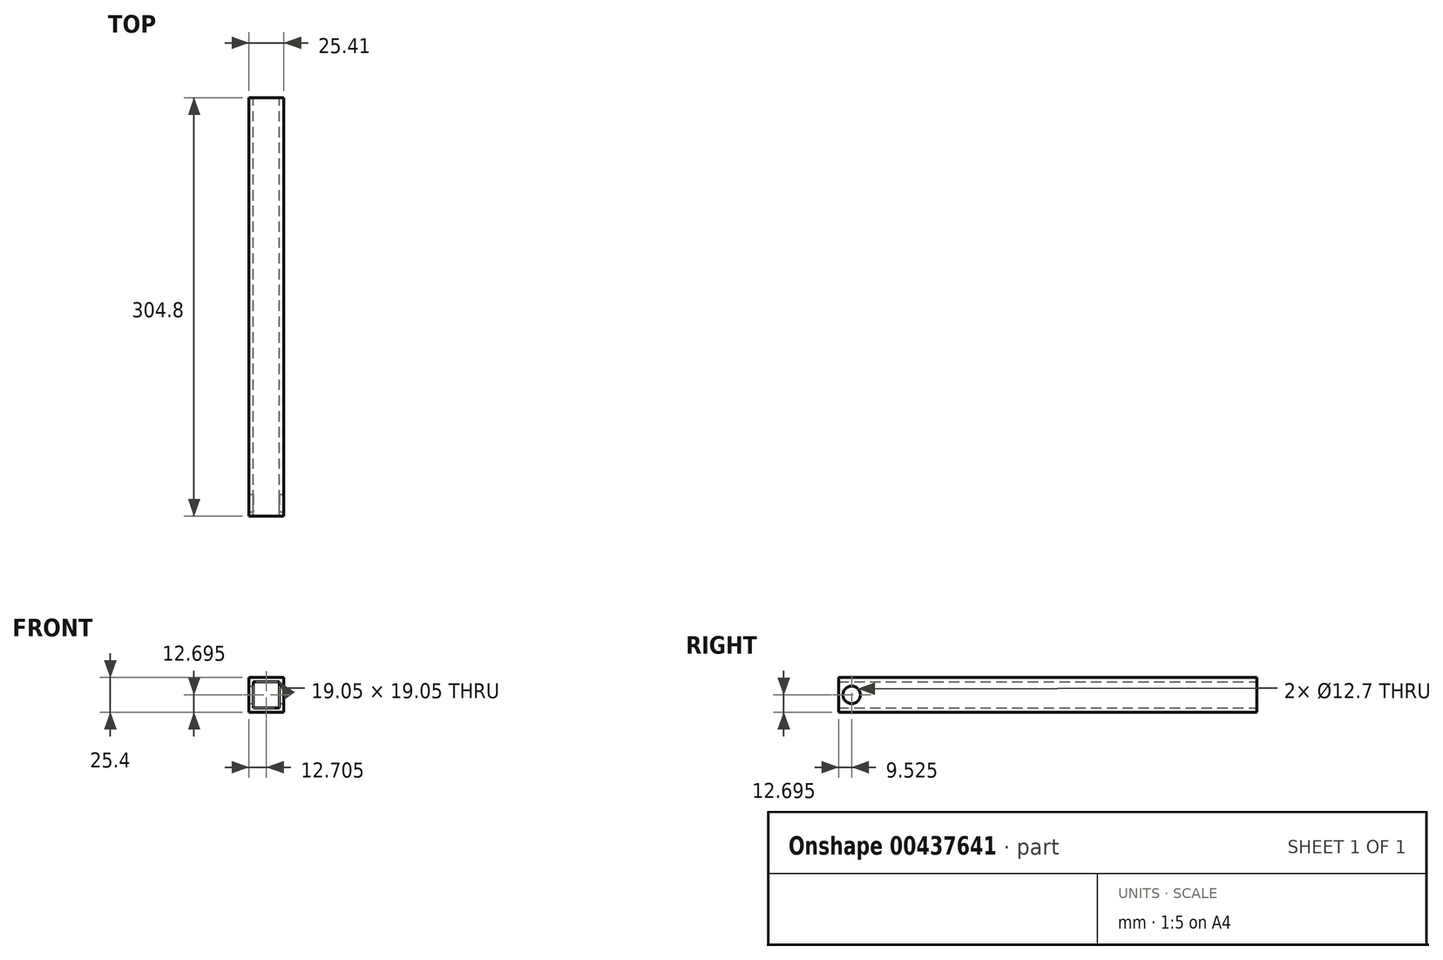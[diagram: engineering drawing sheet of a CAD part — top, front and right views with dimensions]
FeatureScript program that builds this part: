
annotation { "Feature Type Name" : "Feature", "Feature Type Description" : "" }
export const myFeature = defineFeature(function(context is Context, id is Id, definition is map)
    precondition{}
    {
        {
            var Q0;
            Q0=qCreatedBy(makeId("Front.planeOp"),FACE);
            var sketch = newSketch(context, id + "F0", { "sketchPlane" : qUnion([Q0])});
            skLineSegment(sketch, "E0.bottom", {"start": v(-22.23, 22.23) * mm, "end": v(3.17, 22.23) * mm});
            skLineSegment(sketch, "E0.top", {"start": v(-22.23, -3.18) * mm, "end": v(3.18, -3.18) * mm});
            skLineSegment(sketch, "E0.left", {"start": v(-22.23, 22.23) * mm, "end": v(-22.23, -3.18) * mm});
            skLineSegment(sketch, "E0.right", {"start": v(3.17, 22.23) * mm, "end": v(3.18, -3.18) * mm});
            skLineSegment(sketch, "E1.bottom", {"start": v(-19.05, 19.05) * mm, "end": v(0, 19.05) * mm});
            skLineSegment(sketch, "E1.top", {"start": v(-19.05, 0) * mm, "end": v(0, 0) * mm});
            skLineSegment(sketch, "E1.left", {"start": v(-19.05, 19.05) * mm, "end": v(-19.05, 0) * mm});
            skLineSegment(sketch, "E1.right", {"start": v(0, 19.05) * mm, "end": v(0, 0) * mm});
            skSolve(sketch);
        }
        {
            var Q0;
            Q0=qSketchRegion(id+"F0",true);
            extrude(context, id + "F1", {"entities" : qUnion([Q0]), "depth" : 304.8 * mm});
        }
        {
            var Q0;
            Q0=makeQuery(id+"F1.opExtrude","SWEPT_FACE",FACE,{"disambiguationData":[OSD([sQuery(id+"F0.wireOp",EDGE,"E0.right")])]});
            var sketch = newSketch(context, id + "F2", { "sketchPlane" : qUnion([Q0])});
            skLineSegment(sketch, "E2.bottom", {"start": v(-304.8, 22.23) * mm, "end": v(-295.28, 22.23) * mm});
            skLineSegment(sketch, "E2.top", {"start": v(-304.8, 9.52) * mm, "end": v(-295.28, 9.52) * mm});
            skLineSegment(sketch, "E2.left", {"start": v(-304.8, 22.23) * mm, "end": v(-304.8, 9.52) * mm});
            skLineSegment(sketch, "E2.right", {"start": v(-295.28, 22.23) * mm, "end": v(-295.28, 9.52) * mm});
            skSolve(sketch);
        }
        {
            var Q0;
            Q0=sQuery(id+"F2.wireOp",VERTEX,"HHmvUL8G-0XSV-ua7Z-FtjQ-vSaVrf7iGfoh.top.end");
            var Q1;
            Q1=sQuery(id+"F2.wireOp",VERTEX,"E2.top.end");
            var Q2;
            Q2=makeQuery(id+"F1.opExtrude","SWEPT_BODY",BODY,{"disambiguationData":[OSD([sQuery(id+"F0.wireOp",EDGE,"E0.bottom"),sQuery(id+"F0.wireOp",EDGE,"E0.top"),sQuery(id+"F0.wireOp",EDGE,"E0.left"),sQuery(id+"F0.wireOp",EDGE,"E0.right"),sQuery(id+"F0.wireOp",EDGE,"E1.bottom"),sQuery(id+"F0.wireOp",EDGE,"E1.top"),sQuery(id+"F0.wireOp",EDGE,"E1.left"),sQuery(id+"F0.wireOp",EDGE,"E1.right")])]});
            hole(context, id + "F3", {"style" : HoleStyle.SIMPLE, "endStyle" : HoleEndStyle.THROUGH, "holeDiameter" : 12.7 * mm, "isTappedThrough" : true, "tappedDepth" : 12.7 * mm, "tapClearance" : 3, "startFromSketch" : true, "locations" : qUnion([Q0, Q1]), "scope" : qUnion([Q2])});
        }
    });
